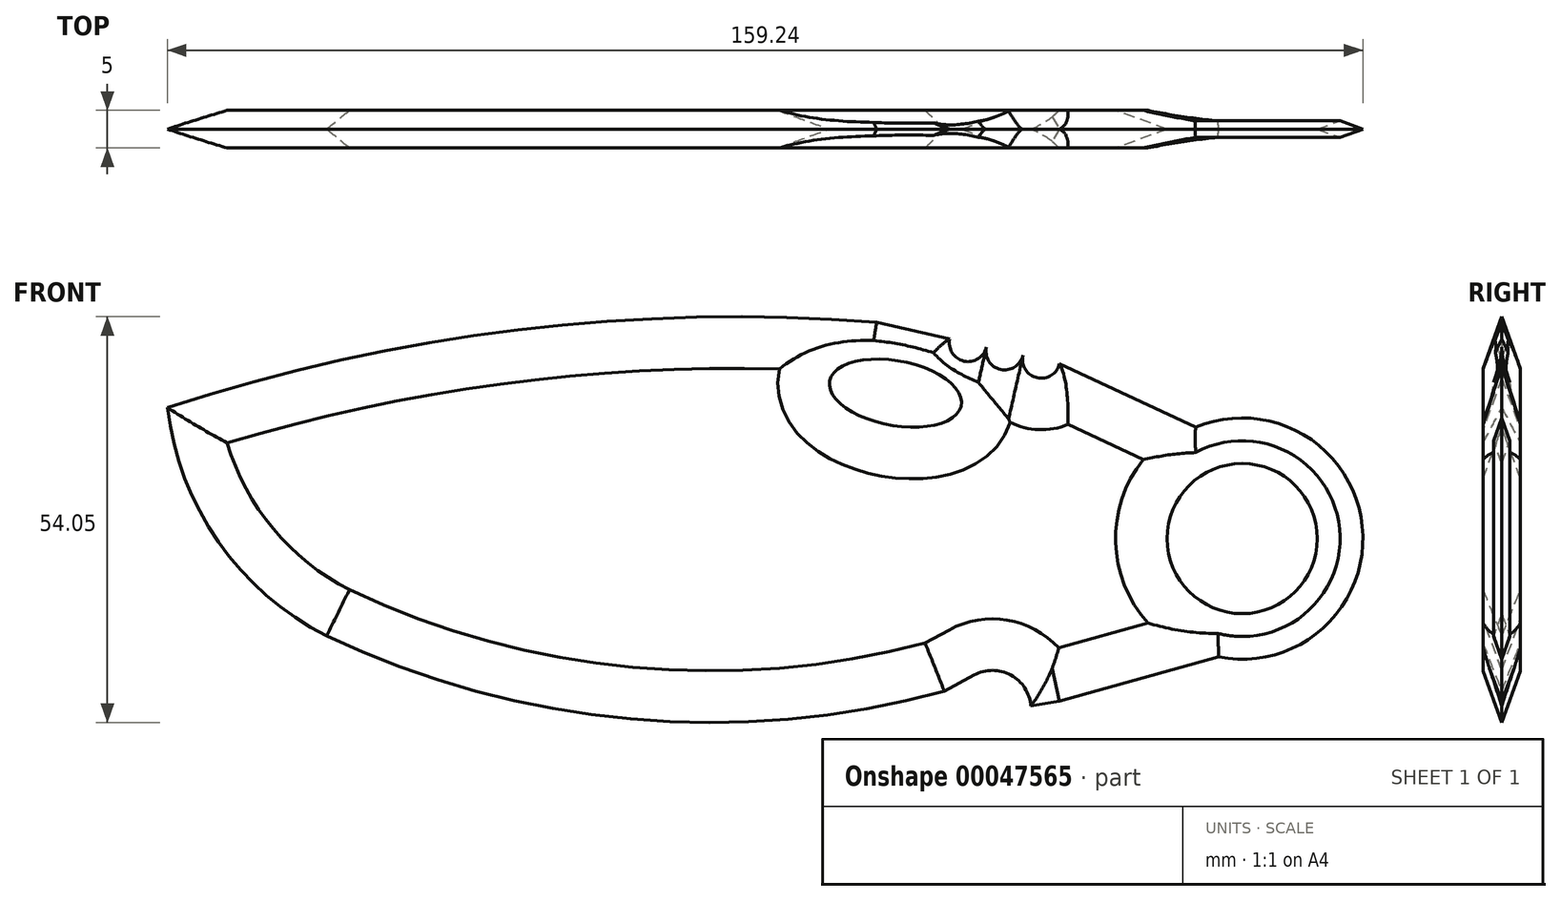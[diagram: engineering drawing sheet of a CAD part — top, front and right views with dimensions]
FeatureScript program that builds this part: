
annotation { "Feature Type Name" : "Feature", "Feature Type Description" : "" }
export const myFeature = defineFeature(function(context is Context, id is Id, definition is map)
    precondition{}
    {
        {
            var Q0;
            Q0=qCreatedBy(makeId("Front.planeOp"),FACE);
            var sketch = newSketch(context, id + "F0", { "sketchPlane" : qUnion([Q0])});
            skLineSegment(sketch, "E0", {"start": v(0, 0) * mm, "end": v(3.59, 9.33) * mm});
            skLineSegment(sketch, "E1", {"start": v(0, -22.5) * mm, "end": v(0, 22.5) * mm});
            skLineSegment(sketch, "E2", {"start": v(0, 22.5) * mm, "end": v(0, 0) * mm});
            skPoint(sketch, "E3.end.orphan", {"position": v(0, 16.37) * mm});
            skLineSegment(sketch, "E4", {"start": v(0, -22.5) * mm, "end": v(-3.84, -23.13) * mm});
            skLineSegment(sketch, "E5", {"start": v(-14.63, 25.8) * mm, "end": v(-24.38, 28.01) * mm});
            skArc(sketch, "E6", {"start": v(-118.84, 16.61) * mm, "mid": v(-112.06, -1.25) * mm, "end": v(-97.64, -13.8) * mm});
            skLineSegment(sketch, "E7", {"start": v(-118.84, 16.61) * mm, "end": v(0, 0) * mm});
            skPoint(sketch, "E8.end.orphan", {"position": v(-42.34, -13.8) * mm});
            skEllipse(sketch, "E9", {"center": v(-21.87, 18.56) * mm, "majorRadius": 8.92 * mm, "minorRadius": 4.32 * mm, "majorAxis": v(0.98, -0.18)});
            skArc(sketch, "E10", {"start": v(-4.88, 23.6) * mm, "mid": v(-2.99, 20.61) * mm, "end": v(0, 22.5) * mm});
            skArc(sketch, "E11", {"start": v(-9.75, 24.7) * mm, "mid": v(-7.87, 21.72) * mm, "end": v(-4.88, 23.6) * mm});
            skArc(sketch, "E12", {"start": v(-14.63, 25.8) * mm, "mid": v(-12.74, 22.82) * mm, "end": v(-9.75, 24.7) * mm});
            skArc(sketch, "E13", {"start": v(-24.38, 28.01) * mm, "mid": v(-72.18, 26.98) * mm, "end": v(-118.84, 16.61) * mm});
            skLineSegment(sketch, "E14", {"start": v(0, 22.5) * mm, "end": v(18.1, 14) * mm});
            skLineSegment(sketch, "E15", {"start": v(0, -22.5) * mm, "end": v(21.2, -16.59) * mm});
            skArc(sketch, "E16", {"start": v(21.2, -16.59) * mm, "mid": v(40.32, 0.8) * mm, "end": v(18.1, 14) * mm});
            skCircle(sketch, "E17", {"center": v(24.32, -0.82) * mm, "radius": 10 * mm});
            skLineSegment(sketch, "E18", {"start": v(24.32, -0.82) * mm, "end": v(28.18, 8.4) * mm});
            skArc(sketch, "E19", {"start": v(-3.84, -23.13) * mm, "mid": v(-6.5, -19) * mm, "end": v(-11.4, -19.01) * mm});
            skLineSegment(sketch, "E20", {"start": v(-11.4, -19.01) * mm, "end": v(-15.34, -21.17) * mm});
            skArc(sketch, "E21", {"start": v(-97.64, -13.8) * mm, "mid": v(-57.15, -24.85) * mm, "end": v(-15.34, -21.17) * mm});
            skSolve(sketch);
        }
        {
            var Q0;
            Q0 = qSketchRegion(id + "F0", true);
            extrude(context, id + "F1", {"entities" : qUnion([Q0]), "depth" : 2.5 * mm, "hasDraft" : true, "draftAngle" : 70 * degree, "draftPullDirection" : true, "hasSecondDirection" : true, "secondDirectionOppositeDirection" : true, "secondDirectionDepth" : 2.5 * mm, "hasSecondDirectionDraft" : true, "secondDirectionDraftAngle" : 70 * degree, "secondDirectionDraftPullDirection" : true});
        }
    });
